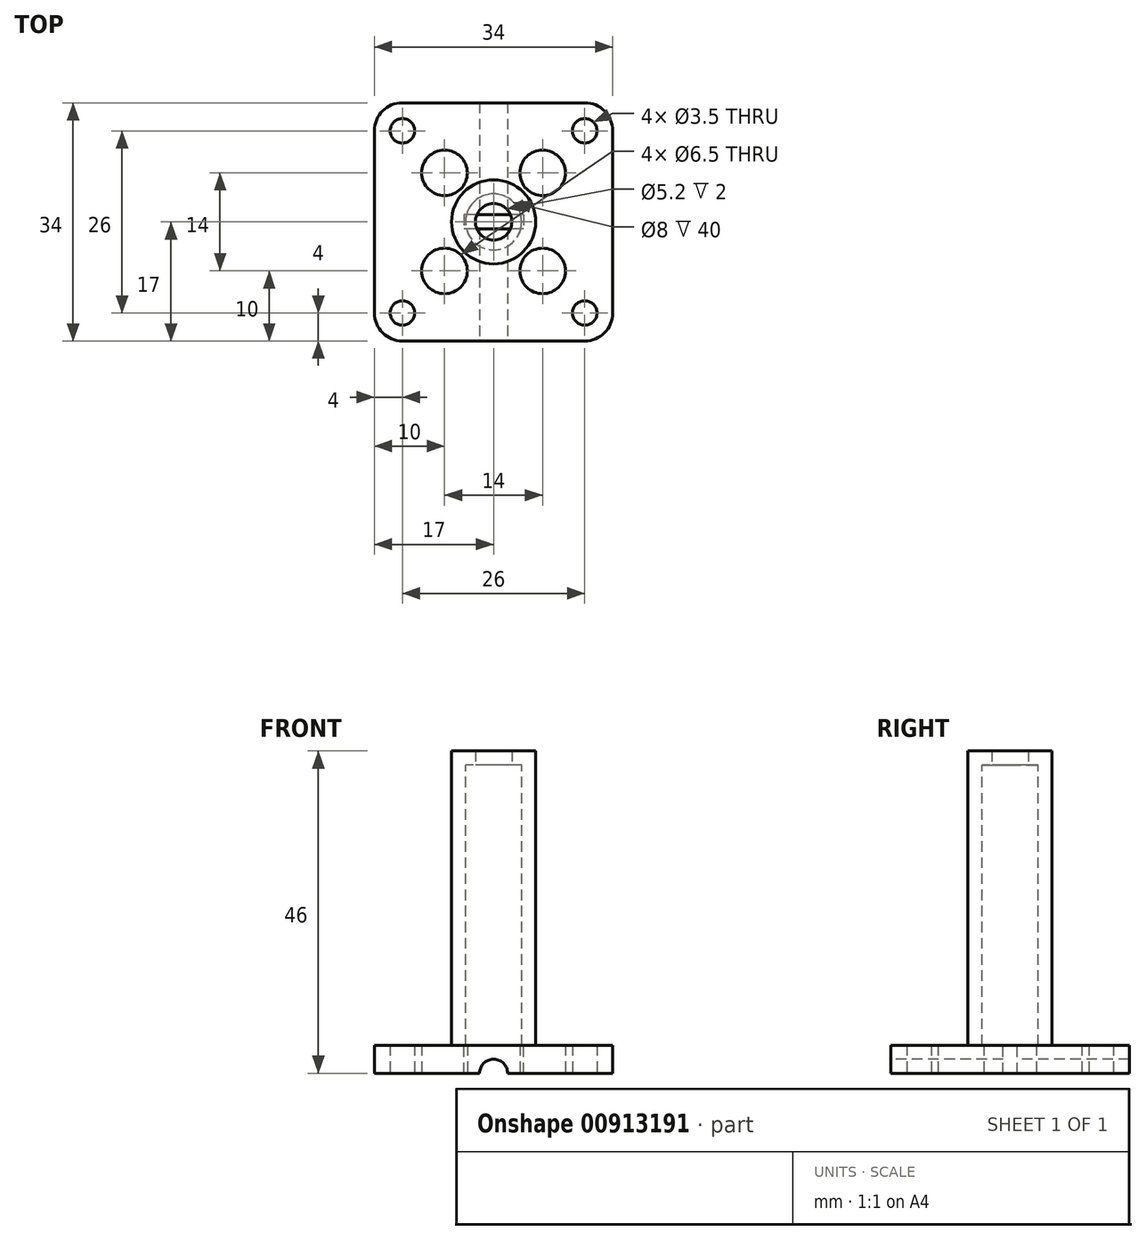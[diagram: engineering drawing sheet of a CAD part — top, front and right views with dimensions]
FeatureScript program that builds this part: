
annotation { "Feature Type Name" : "Feature", "Feature Type Description" : "" }
export const myFeature = defineFeature(function(context is Context, id is Id, definition is map)
    precondition{}
    {
        {
            var Q0;
            Q0=qCreatedBy(makeId("Top.planeOp"),FACE);
            var sketch = newSketch(context, id + "F0", { "sketchPlane" : qUnion([Q0])});
            skCircle(sketch, "E0", {"center": v(-7, 7) * mm, "radius": 3.25 * mm});
            skCircle(sketch, "E1", {"center": v(7, 7) * mm, "radius": 3.25 * mm});
            skCircle(sketch, "E2", {"center": v(7, -7) * mm, "radius": 3.25 * mm});
            skCircle(sketch, "E3", {"center": v(-7, -7) * mm, "radius": 3.25 * mm});
            skCircle(sketch, "E4", {"center": v(-13, 13) * mm, "radius": 1.75 * mm});
            skCircle(sketch, "E5", {"center": v(13, 13) * mm, "radius": 1.75 * mm});
            skCircle(sketch, "E6", {"center": v(13, -13) * mm, "radius": 1.75 * mm});
            skCircle(sketch, "E7", {"center": v(-13, -13) * mm, "radius": 1.75 * mm});
            skArc(sketch, "E8", {"start": v(-13, -17) * mm, "mid": v(-15.83, -15.83) * mm, "end": v(-17, -13) * mm});
            skArc(sketch, "E9", {"start": v(-17, 13) * mm, "mid": v(-15.83, 15.83) * mm, "end": v(-13, 17) * mm});
            skArc(sketch, "E10", {"start": v(13, 17) * mm, "mid": v(15.83, 15.83) * mm, "end": v(17, 13) * mm});
            skArc(sketch, "E11", {"start": v(17, -13) * mm, "mid": v(15.83, -15.83) * mm, "end": v(13, -17) * mm});
            skLineSegment(sketch, "E12", {"start": v(-17, -13) * mm, "end": v(-17, 13) * mm});
            skLineSegment(sketch, "E13", {"start": v(-13, 17) * mm, "end": v(13, 17) * mm});
            skLineSegment(sketch, "E14", {"start": v(17, 13) * mm, "end": v(17, -13) * mm});
            skLineSegment(sketch, "E15", {"start": v(13, -17) * mm, "end": v(-13, -17) * mm});
            skSolve(sketch);
        }
        {
            var Q0;
            Q0=qSketchRegion(id+"F0",true);
            extrude(context, id + "F1", {"entities" : qUnion([Q0]), "depth" : 4 * mm, "offsetDistance" : 25 * mm});
        }
        {
            var Q0;
            Q0=makeQuery(id+"F1.opExtrude","SWEPT_FACE",FACE,{"disambiguationData":[OSD([sQuery(id+"F0.wireOp",EDGE,"E15")])]});
            var sketch = newSketch(context, id + "F2", { "sketchPlane" : qUnion([Q0])});
            skCircle(sketch, "E16", {"center": v(0, 0) * mm, "radius": 2 * mm});
            skSolve(sketch);
        }
        {
            var Q0;
            Q0=qSketchRegion(id+"F2",true);
            extrude(context, id + "F3", {"entities" : qUnion([Q0]), "depth" : -34 * mm, "offsetDistance" : 25 * mm});
        }
        {
            var Q0;
            Q0=makeQuery(id+"F3.opExtrude","SWEPT_BODY",BODY,{"disambiguationData":[OSD([sQuery(id+"F2.wireOp",EDGE,"E16")])]});
            var Q1;
            Q1=makeQuery(id+"F1.opExtrude","SWEPT_BODY",BODY,{"disambiguationData":[OSD([sQuery(id+"F0.wireOp",EDGE,"E0"),sQuery(id+"F0.wireOp",EDGE,"E1"),sQuery(id+"F0.wireOp",EDGE,"E2"),sQuery(id+"F0.wireOp",EDGE,"E3"),sQuery(id+"F0.wireOp",EDGE,"E4"),sQuery(id+"F0.wireOp",EDGE,"E5"),sQuery(id+"F0.wireOp",EDGE,"E6"),sQuery(id+"F0.wireOp",EDGE,"E7"),sQuery(id+"F0.wireOp",EDGE,"E8"),sQuery(id+"F0.wireOp",EDGE,"E9"),sQuery(id+"F0.wireOp",EDGE,"E10"),sQuery(id+"F0.wireOp",EDGE,"E11"),sQuery(id+"F0.wireOp",EDGE,"E12"),sQuery(id+"F0.wireOp",EDGE,"E13"),sQuery(id+"F0.wireOp",EDGE,"E14"),sQuery(id+"F0.wireOp",EDGE,"E15")])]});
            booleanBodies(context, id + "F4", {"operationType" : BooleanOperationType.SUBTRACTION, "tools" : qUnion([Q0]), "targets" : qUnion([Q1])});
        }
        {
            var Q0;
            Q0=makeQuery(id+"F1.opExtrude","CAP_FACE",FACE,{"disambiguationData":[OSD([sQuery(id+"F0.wireOp",EDGE,"E0"),sQuery(id+"F0.wireOp",EDGE,"E1"),sQuery(id+"F0.wireOp",EDGE,"E2"),sQuery(id+"F0.wireOp",EDGE,"E3"),sQuery(id+"F0.wireOp",EDGE,"E4"),sQuery(id+"F0.wireOp",EDGE,"E5"),sQuery(id+"F0.wireOp",EDGE,"E6"),sQuery(id+"F0.wireOp",EDGE,"E7"),sQuery(id+"F0.wireOp",EDGE,"E8"),sQuery(id+"F0.wireOp",EDGE,"E9"),sQuery(id+"F0.wireOp",EDGE,"E10"),sQuery(id+"F0.wireOp",EDGE,"E11"),sQuery(id+"F0.wireOp",EDGE,"E12"),sQuery(id+"F0.wireOp",EDGE,"E13"),sQuery(id+"F0.wireOp",EDGE,"E14"),sQuery(id+"F0.wireOp",EDGE,"E15")])],"isStart":false});
            var sketch = newSketch(context, id + "F5", { "sketchPlane" : qUnion([Q0])});
            skCircle(sketch, "E17", {"center": v(0, 0) * mm, "radius": 6 * mm});
            skSolve(sketch);
        }
        {
            var Q0;
            Q0=qSketchRegion(id+"F5",true);
            extrude(context, id + "F6", {"entities" : qUnion([Q0]), "operationType" : NewBodyOperationType.ADD, "depth" : 40 * mm, "offsetDistance" : 25 * mm});
        }
        {
            var Q0;
            Q0=makeQuery(id+"F6.opExtrude","CAP_FACE",FACE,{"disambiguationData":[OSD([sQuery(id+"F5.wireOp",EDGE,"E17")])],"isStart":false});
            var sketch = newSketch(context, id + "F7", { "sketchPlane" : qUnion([Q0])});
            skCircle(sketch, "E18", {"center": v(0, 0) * mm, "radius": 4 * mm});
            skSolve(sketch);
        }
        {
            var Q0;
            Q0=qSketchRegion(id+"F7",true);
            extrude(context, id + "F8", {"entities" : qUnion([Q0]), "depth" : -40 * mm, "offsetDistance" : 25 * mm});
        }
        {
            var Q0;
            Q0=makeQuery(id+"F8.opExtrude","SWEPT_BODY",BODY,{"disambiguationData":[OSD([sQuery(id+"F7.wireOp",EDGE,"E18")])]});
            var Q1;
            Q1=makeQuery(id+"F1.opExtrude","SWEPT_BODY",BODY,{"disambiguationData":[OSD([sQuery(id+"F0.wireOp",EDGE,"E0"),sQuery(id+"F0.wireOp",EDGE,"E1"),sQuery(id+"F0.wireOp",EDGE,"E2"),sQuery(id+"F0.wireOp",EDGE,"E3"),sQuery(id+"F0.wireOp",EDGE,"E4"),sQuery(id+"F0.wireOp",EDGE,"E5"),sQuery(id+"F0.wireOp",EDGE,"E6"),sQuery(id+"F0.wireOp",EDGE,"E7"),sQuery(id+"F0.wireOp",EDGE,"E8"),sQuery(id+"F0.wireOp",EDGE,"E9"),sQuery(id+"F0.wireOp",EDGE,"E10"),sQuery(id+"F0.wireOp",EDGE,"E11"),sQuery(id+"F0.wireOp",EDGE,"E12"),sQuery(id+"F0.wireOp",EDGE,"E13"),sQuery(id+"F0.wireOp",EDGE,"E14"),sQuery(id+"F0.wireOp",EDGE,"E15")])]});
            booleanBodies(context, id + "F9", {"operationType" : BooleanOperationType.SUBTRACTION, "tools" : qUnion([Q0]), "targets" : qUnion([Q1])});
        }
        {
            var Q0;
            Q0=makeQuery(id+"F6.opExtrude","CAP_FACE",FACE,{"disambiguationData":[OSD([sQuery(id+"F5.wireOp",EDGE,"E17")])],"isStart":false});
            var sketch = newSketch(context, id + "F10", { "sketchPlane" : qUnion([Q0])});
            skCircle(sketch, "E19", {"center": v(0, 0) * mm, "radius": 6 * mm});
            skCircle(sketch, "E20", {"center": v(0, 0) * mm, "radius": 2.6 * mm});
            skSolve(sketch);
        }
        {
            var Q0;
            Q0=qSketchRegion(id+"F10",true);
            extrude(context, id + "F11", {"entities" : qUnion([Q0]), "operationType" : NewBodyOperationType.ADD, "depth" : 2 * mm, "offsetDistance" : 25 * mm});
        }
        {
            var Q0;
            Q0=makeQuery(id+"F1.opExtrude","CAP_FACE",FACE,{"disambiguationData":[OSD([sQuery(id+"F0.wireOp",EDGE,"E0"),sQuery(id+"F0.wireOp",EDGE,"E1"),sQuery(id+"F0.wireOp",EDGE,"E2"),sQuery(id+"F0.wireOp",EDGE,"E3"),sQuery(id+"F0.wireOp",EDGE,"E4"),sQuery(id+"F0.wireOp",EDGE,"E5"),sQuery(id+"F0.wireOp",EDGE,"E6"),sQuery(id+"F0.wireOp",EDGE,"E7"),sQuery(id+"F0.wireOp",EDGE,"E8"),sQuery(id+"F0.wireOp",EDGE,"E9"),sQuery(id+"F0.wireOp",EDGE,"E10"),sQuery(id+"F0.wireOp",EDGE,"E11"),sQuery(id+"F0.wireOp",EDGE,"E12"),sQuery(id+"F0.wireOp",EDGE,"E13"),sQuery(id+"F0.wireOp",EDGE,"E14"),sQuery(id+"F0.wireOp",EDGE,"E15")])],"isStart":false});
            var sketch = newSketch(context, id + "F12", { "sketchPlane" : qUnion([Q0])});
            skLineSegment(sketch, "E21.bottom", {"start": v(4.25, 1) * mm, "end": v(-4.25, 1) * mm});
            skLineSegment(sketch, "E21.top", {"start": v(4.25, -1) * mm, "end": v(-4.25, -1) * mm});
            skLineSegment(sketch, "E21.left", {"start": v(4.25, 1) * mm, "end": v(4.25, -1) * mm});
            skLineSegment(sketch, "E21.right", {"start": v(-4.25, 1) * mm, "end": v(-4.25, -1) * mm});
            skPoint(sketch, "E21.middle", {"position": v(0, 0) * mm});
            skSolve(sketch);
        }
        {
            var Q0;
            Q0=qSketchRegion(id+"F12",true);
            extrude(context, id + "F13", {"entities" : qUnion([Q0]), "depth" : -10 * mm, "offsetDistance" : 25 * mm});
        }
        {
            var Q0;
            Q0=makeQuery(id+"F13.opExtrude","SWEPT_BODY",BODY,{"disambiguationData":[OSD([sQuery(id+"F12.wireOp",EDGE,"E21.bottom"),sQuery(id+"F12.wireOp",EDGE,"E21.top"),sQuery(id+"F12.wireOp",EDGE,"E21.left"),sQuery(id+"F12.wireOp",EDGE,"E21.right")])]});
            var Q1;
            Q1=makeQuery(id+"F1.opExtrude","SWEPT_BODY",BODY,{"disambiguationData":[OSD([sQuery(id+"F0.wireOp",EDGE,"E0"),sQuery(id+"F0.wireOp",EDGE,"E1"),sQuery(id+"F0.wireOp",EDGE,"E2"),sQuery(id+"F0.wireOp",EDGE,"E3"),sQuery(id+"F0.wireOp",EDGE,"E4"),sQuery(id+"F0.wireOp",EDGE,"E5"),sQuery(id+"F0.wireOp",EDGE,"E6"),sQuery(id+"F0.wireOp",EDGE,"E7"),sQuery(id+"F0.wireOp",EDGE,"E8"),sQuery(id+"F0.wireOp",EDGE,"E9"),sQuery(id+"F0.wireOp",EDGE,"E10"),sQuery(id+"F0.wireOp",EDGE,"E11"),sQuery(id+"F0.wireOp",EDGE,"E12"),sQuery(id+"F0.wireOp",EDGE,"E13"),sQuery(id+"F0.wireOp",EDGE,"E14"),sQuery(id+"F0.wireOp",EDGE,"E15")])]});
            booleanBodies(context, id + "F14", {"operationType" : BooleanOperationType.SUBTRACTION, "tools" : qUnion([Q0]), "targets" : qUnion([Q1])});
        }
    });
